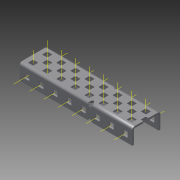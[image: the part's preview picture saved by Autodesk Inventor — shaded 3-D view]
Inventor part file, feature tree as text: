
AUTODESK INVENTOR PART (.ipt)
format: ipt  version: 2015 (Build 190159000, 159)  size: 1,985,024 bytes
history: native  units: in
note: dims shown in document units (in); Inventor stores cm internally (conversion verified against a paired STEP export)
features: other x46, pattern_linear x3, sheet_metal_op x1, extrude x1, imported_body x1, sketch x1
ambient origin geometry x8: Origin, YZ Plane, XZ Plane, XY Plane, X Axis, Y Axis, Z Axis, Center Point
bodies: Body1 (feature_tree)
feature tree (53):
  sheet_metal_op  "Fold1"
  other  "C-Channel"
  extrude  "length cut"  Depth=0.5in
  other  "top axis"
  other  "inner axis"
  other  "front axis"
  other  "back axis"
  pattern_linear  "top axes"  Spacing1=0.5in  [1 undecoded]
  pattern_linear  "inner axes"  Spacing1=0.5in  [1 undecoded]
  pattern_linear  "horiz axes"  Spacing1=-4.0in  [1 undecoded]
  other  "right plane"
  imported_body  "Base1"
  sketch  "Sketch1"  dims[d1=0.0in d4=0.5in d5=0.7874in d7=0.5in d10=0.5in d13=0.5in d14=-4.0in d15=0.0in d16=0.0in d17=0.0in d18=0.0in d19=0.0in]
  other  "Work Point1"
  other  "Work Point2"
  other  "Work Point3"
  other  "Work Point4"
  other  "Work Axis5"
  other  "Work Axis6"
  other  "Work Axis7"
  other  "Work Axis8"
  other  "Work Axis11"
  other  "Work Axis12"
  other  "Work Axis13"
  other  "Work Axis14"
  other  "Work Axis15"
  other  "Work Axis18"
  other  "Work Axis19"
  other  "Work Axis20"
  other  "Work Axis23"
  other  "Work Axis24"
  other  "Work Axis25"
  other  "Work Axis26"
  other  "Work Axis30"
  other  "Work Axis31"
  other  "Work Axis32"
  other  "Work Axis33"
  other  "left plane"
  other  "Work Axis137"
  other  "Work Axis138"
  other  "Work Axis142"
  other  "Work Axis143"
  other  "Work Axis147"
  other  "Work Axis148"
  other  "Work Axis152"
  other  "Work Axis153"
  other  "Work Axis157"
  other  "Work Axis158"
  other  "Work Axis162"
  other  "Work Axis163"
  other  "Work Axis164"
  other  "Work Axis165"
  other  "Work Axis166"
note: 3 required parameter values undecoded (feature->parameter linkage not recoverable at this tier; creation-order binding heuristic only, values carry confidence <= 0.55)
